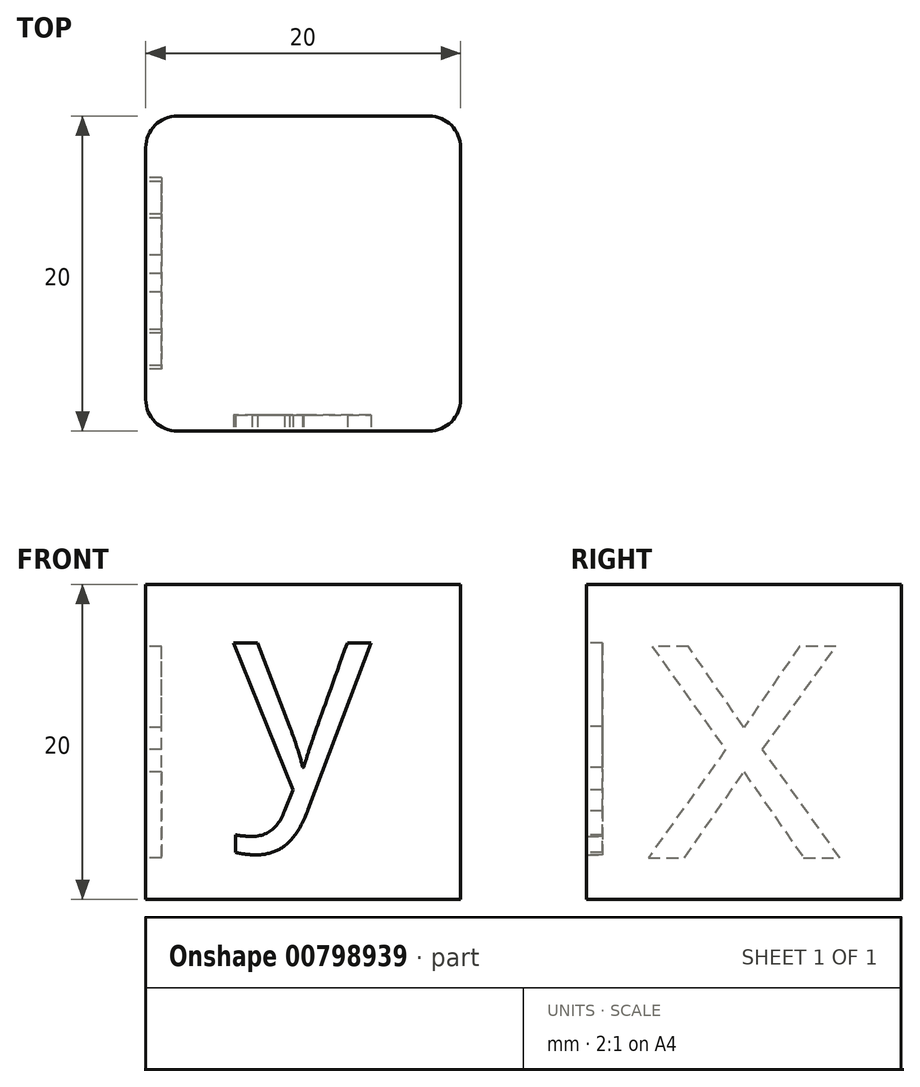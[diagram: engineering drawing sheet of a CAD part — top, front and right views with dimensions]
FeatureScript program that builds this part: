
annotation { "Feature Type Name" : "Feature", "Feature Type Description" : "" }
export const myFeature = defineFeature(function(context is Context, id is Id, definition is map)
    precondition{}
    {
        {
            var Q0;
            Q0=qCreatedBy(makeId("Top.planeOp"),FACE);
            var sketch = newSketch(context, id + "F0", { "sketchPlane" : qUnion([Q0])});
            skLineSegment(sketch, "E0.bottom", {"start": v(-10, 10) * mm, "end": v(10, 10) * mm});
            skLineSegment(sketch, "E0.top", {"start": v(-10, -10) * mm, "end": v(10, -10) * mm});
            skLineSegment(sketch, "E0.left", {"start": v(-10, 10) * mm, "end": v(-10, -10) * mm});
            skLineSegment(sketch, "E0.right", {"start": v(10, 10) * mm, "end": v(10, -10) * mm});
            skPoint(sketch, "E0.middle", {"position": v(0, 0) * mm});
            skSolve(sketch);
        }
        {
            var Q0;
            Q0 = qSketchRegion(id + "F0", true);
            extrude(context, id + "F1", {"entities" : qUnion([Q0]), "depth" : 20 * mm, "offsetDistance" : 25 * mm});
        }
        {
            var Q0;
            Q0=makeQuery(id+"F1.opExtrude","SWEPT_EDGE",EDGE,{"disambiguationData":[OSD([sQuery(id+"F0.wireOp",EDGE,"E0.top"),sQuery(id+"F0.wireOp",EDGE,"E0.left")])]});
            var Q1;
            Q1=makeQuery(id+"F1.opExtrude","SWEPT_EDGE",EDGE,{"disambiguationData":[OSD([sQuery(id+"F0.wireOp",EDGE,"E0.bottom"),sQuery(id+"F0.wireOp",EDGE,"E0.left")])]});
            var Q2;
            Q2=makeQuery(id+"F1.opExtrude","SWEPT_EDGE",EDGE,{"disambiguationData":[OSD([sQuery(id+"F0.wireOp",EDGE,"E0.top"),sQuery(id+"F0.wireOp",EDGE,"E0.right")])]});
            var Q3;
            Q3=makeQuery(id+"F1.opExtrude","SWEPT_EDGE",EDGE,{"disambiguationData":[OSD([sQuery(id+"F0.wireOp",EDGE,"E0.bottom"),sQuery(id+"F0.wireOp",EDGE,"E0.right")])]});
            fillet(context, id + "F2", {"entities" : qUnion([Q0, Q1, Q2, Q3]), "radius" : 2 * mm, "tangentPropagation" : true, "allowEdgeOverflow" : false});
        }
        {
            var Q0;
            Q0=makeQuery(id+"F1.opExtrude","SWEPT_FACE",FACE,{"disambiguationData":[OSD([sQuery(id+"F0.wireOp",EDGE,"E0.left")])]});
            var sketch = newSketch(context, id + "F3", { "sketchPlane" : qUnion([Q0])});
            skText(sketch, "E1", { "text": "x", "fontName": "OpenSans-Regular.ttf"});
            skLineSegment(sketch, "E2", {"start": v(0, 0) * mm, "end": v(0, 20) * mm, "construction": true});
            const initialGuessF3  = {"E1": [-0.00657, 0.00264, 1, 0, 0.01807]};
            skSetInitialGuess(sketch, initialGuessF3);
            skSolve(sketch);
        }
        {
            var Q0;
            Q0 = qSketchRegion(id + "F3", true);
            extrude(context, id + "F4", {"entities" : qUnion([Q0]), "operationType" : NewBodyOperationType.REMOVE, "oppositeDirection" : true, "depth" : 1 * mm, "offsetDistance" : 25 * mm});
        }
        {
            var Q0;
            Q0=makeQuery(id+"F1.opExtrude","SWEPT_FACE",FACE,{"disambiguationData":[OSD([sQuery(id+"F0.wireOp",EDGE,"E0.top")])]});
            var sketch = newSketch(context, id + "F5", { "sketchPlane" : qUnion([Q0])});
            skText(sketch, "E3", { "text": "y", "fontName": "OpenSans-Regular.ttf"});
            const initialGuessF5  = {"E3": [-0.00442, 0.007, 1, 0, 0.0125]};
            skSetInitialGuess(sketch, initialGuessF5);
            skSolve(sketch);
        }
        {
            var Q0;
            Q0 = qSketchRegion(id + "F5", true);
            extrude(context, id + "F6", {"entities" : qUnion([Q0]), "operationType" : NewBodyOperationType.REMOVE, "oppositeDirection" : true, "depth" : 1 * mm, "offsetDistance" : 25 * mm});
        }
    });
